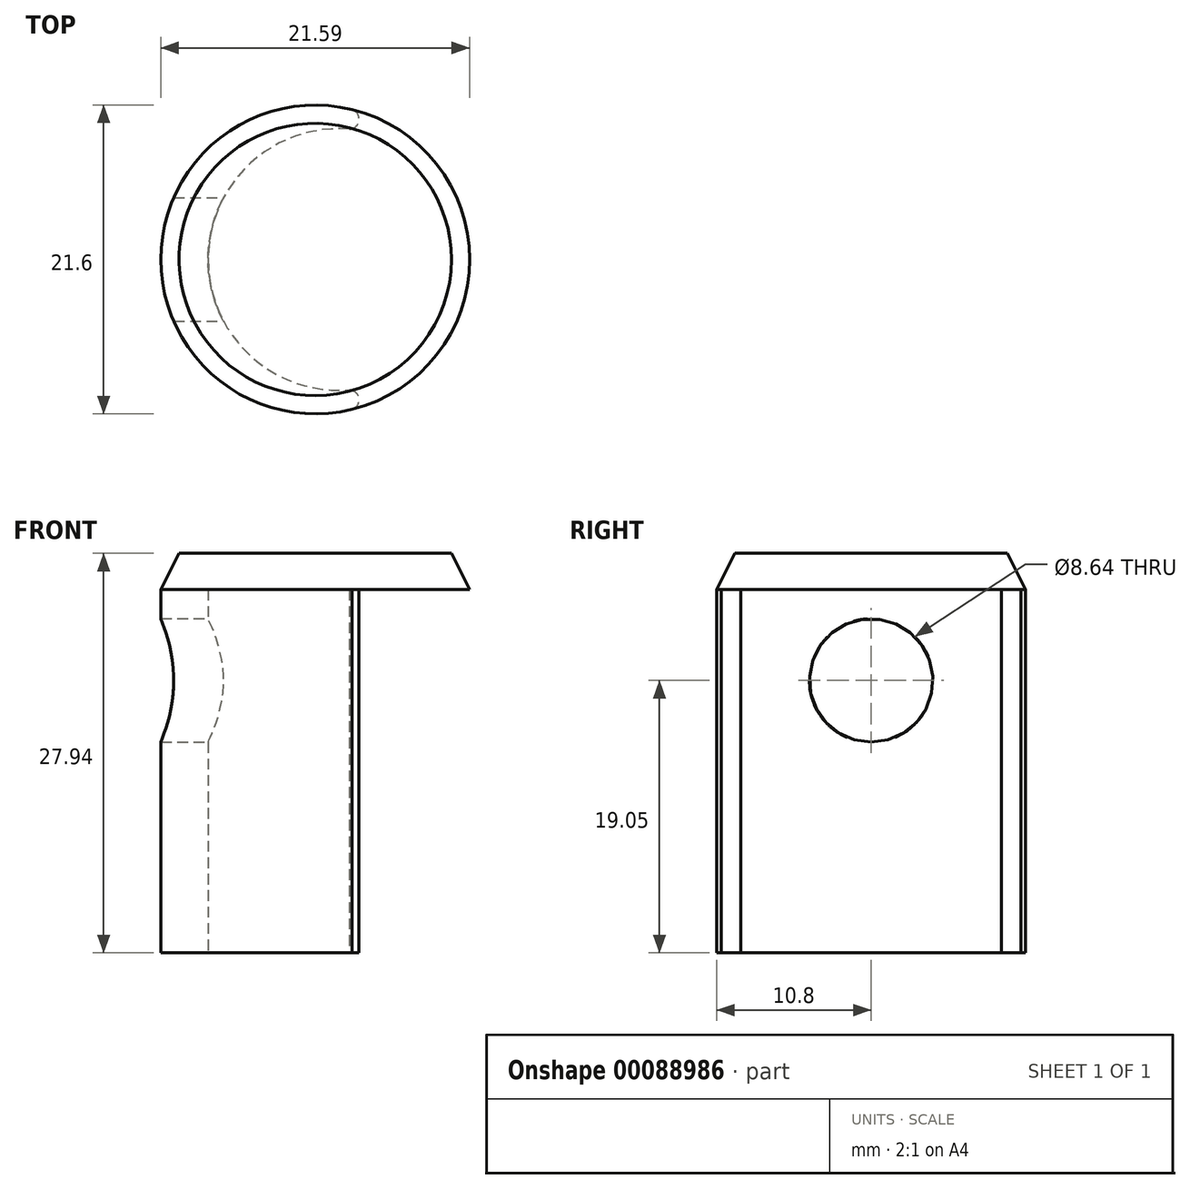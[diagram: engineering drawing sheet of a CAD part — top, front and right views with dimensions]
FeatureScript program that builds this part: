
annotation { "Feature Type Name" : "Feature", "Feature Type Description" : "" }
export const myFeature = defineFeature(function(context is Context, id is Id, definition is map)
    precondition{}
    {
        {
            var Q0;
            Q0=qCreatedBy(makeId("Top.planeOp"),FACE);
            var sketch = newSketch(context, id + "F0", { "sketchPlane" : qUnion([Q0])});
            skArc(sketch, "E0", {"start": v(0.73, 9.11) * mm, "mid": v(-9.14, 0) * mm, "end": v(0.73, -9.11) * mm});
            skArc(sketch, "E1", {"start": v(0.92, 10.48) * mm, "mid": v(-12.45, 0) * mm, "end": v(0.92, -10.48) * mm});
            skLineSegment(sketch, "E2", {"start": v(9.1, 7.69) * mm, "end": v(9.18, -6.9) * mm, "construction": true});
            skArc(sketch, "E3", {"start": v(0.73, 9.11) * mm, "mid": v(1.4, 9.72) * mm, "end": v(0.92, 10.48) * mm});
            skArc(sketch, "E4.MirrorCS", {"start": v(0.73, -9.11) * mm, "mid": v(1.4, -9.72) * mm, "end": v(0.92, -10.48) * mm});
            skPoint(sketch, "E5.orphan", {"position": v(0.82, 10.5) * mm});
            skPoint(sketch, "E6.orphan", {"position": v(0.82, -10.5) * mm});
            skSolve(sketch);
        }
        {
            var Q0;
            Q0=makeQuery(id+"F0.imprint","IMPRINT",FACE,{"disambiguationData":[TD([[makeQuery(id+"F0.imprint","IMPRINT",EDGE,{"derivedFrom":sQuery(id+"F0.wireOp",EDGE,"E0")}),-1.0]])]});
            extrude(context, id + "F1", {"entities" : qUnion([Q0]), "depth" : 25.4 * mm});
        }
        {
            var Q0;
            Q0=makeQuery(id+"F1.opExtrude","CAP_FACE",FACE,{"disambiguationData":[OSD([sQuery(id+"F0.wireOp",EDGE,"E0"),sQuery(id+"F0.wireOp",EDGE,"E1"),sQuery(id+"F0.wireOp",EDGE,"E3"),sQuery(id+"F0.wireOp",EDGE,"E4.MirrorCS")])],"isStart":false});
            var sketch = newSketch(context, id + "F2", { "sketchPlane" : qUnion([Q0])});
            skCircle(sketch, "E7", {"center": v(-1.65, 0) * mm, "radius": 10.8 * mm});
            skSolve(sketch);
        }
        {
            var Q0;
            Q0 = qSketchRegion(id + "F2", true);
            extrude(context, id + "F3", {"entities" : qUnion([Q0]), "operationType" : NewBodyOperationType.ADD, "depth" : 2.54 * mm});
        }
        {
            var Q0;
            Q0=qCreatedBy(makeId("Right.planeOp"),FACE);
            var sketch = newSketch(context, id + "F4", { "sketchPlane" : qUnion([Q0])});
            skPoint(sketch, "E8", {"position": v(0, 19.05) * mm});
            skSolve(sketch);
        }
        {
            var Q0;
            Q0=sQuery(id+"F4.wireOp",VERTEX,"E8");
            var Q1;
            Q1=makeQuery(id+"F1.opExtrude","SWEPT_BODY",BODY,{"disambiguationData":[OSD([sQuery(id+"F0.wireOp",EDGE,"E0"),sQuery(id+"F0.wireOp",EDGE,"E1"),sQuery(id+"F0.wireOp",EDGE,"E3"),sQuery(id+"F0.wireOp",EDGE,"E4.MirrorCS")])]});
            hole(context, id + "F5", {"style" : HoleStyle.SIMPLE, "endStyle" : HoleEndStyle.THROUGH, "holeDiameter" : 8.64 * mm, "locations" : qUnion([Q0]), "scope" : qUnion([Q1]), "isTappedThrough" : true});
        }
        {
            var Q0;
            Q0=makeQuery(id+"F3.opExtrude","CAP_EDGE",EDGE,{"disambiguationData":[OSD([sQuery(id+"F2.wireOp",EDGE,"E7")])],"isStart":false});
            chamfer(context, id + "F6", {"entities" : qUnion([Q0]), "chamferType" : ChamferType.TWO_OFFSETS, "width1" : 1.27 * mm, "oppositeDirection" : false, "width2" : 2.54 * mm, "tangentPropagation" : true});
        }
    });
